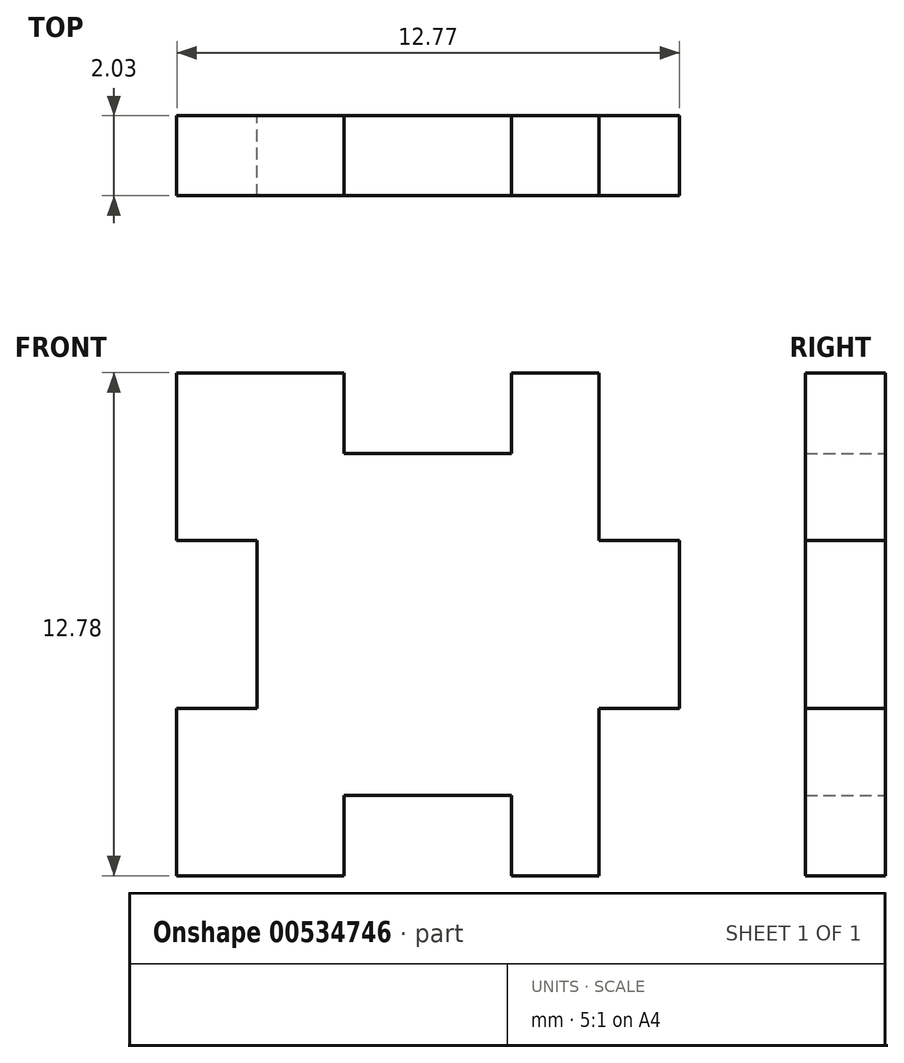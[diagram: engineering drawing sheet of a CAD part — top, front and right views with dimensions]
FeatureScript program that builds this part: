
annotation { "Feature Type Name" : "Feature", "Feature Type Description" : "" }
export const myFeature = defineFeature(function(context is Context, id is Id, definition is map)
    precondition{}
    {
        {
            var Q0;
            Q0=qCreatedBy(makeId("Front.planeOp"),FACE);
            var sketch = newSketch(context, id + "F0", { "sketchPlane" : qUnion([Q0])});
            skLineSegment(sketch, "E0", {"start": v(-10.99, 26.89) * mm, "end": v(-10.99, 29.02) * mm});
            skLineSegment(sketch, "E1", {"start": v(-10.99, 29.02) * mm, "end": v(-13.03, 29.02) * mm});
            skLineSegment(sketch, "E2", {"start": v(-13.03, 29.02) * mm, "end": v(-13.03, 33.28) * mm});
            skLineSegment(sketch, "E3", {"start": v(-13.03, 33.28) * mm, "end": v(-8.78, 33.28) * mm});
            skLineSegment(sketch, "E4", {"start": v(-8.78, 33.28) * mm, "end": v(-8.78, 31.23) * mm});
            skLineSegment(sketch, "E5", {"start": v(-8.78, 31.23) * mm, "end": v(-4.53, 31.23) * mm});
            skLineSegment(sketch, "E6", {"start": v(-4.53, 31.23) * mm, "end": v(-4.53, 33.28) * mm});
            skLineSegment(sketch, "E7", {"start": v(-4.53, 33.28) * mm, "end": v(-2.3, 33.28) * mm});
            skLineSegment(sketch, "E8", {"start": v(-2.3, 33.28) * mm, "end": v(-2.3, 29.02) * mm});
            skLineSegment(sketch, "E9", {"start": v(-2.3, 29.02) * mm, "end": v(-0.26, 29.02) * mm});
            skLineSegment(sketch, "E10", {"start": v(-10.99, 26.89) * mm, "end": v(8.72, 26.89) * mm, "construction": true});
            skLineSegment(sketch, "E11.MirrorCS", {"start": v(-2.3, 24.76) * mm, "end": v(-0.26, 24.76) * mm});
            skLineSegment(sketch, "E12.MirrorCS", {"start": v(-2.3, 20.5) * mm, "end": v(-2.3, 24.76) * mm});
            skLineSegment(sketch, "E13.MirrorCS", {"start": v(-4.53, 20.5) * mm, "end": v(-2.3, 20.5) * mm});
            skLineSegment(sketch, "E14.MirrorCS", {"start": v(-4.53, 22.55) * mm, "end": v(-4.53, 20.5) * mm});
            skLineSegment(sketch, "E15.MirrorCS", {"start": v(-8.78, 22.55) * mm, "end": v(-4.53, 22.55) * mm});
            skLineSegment(sketch, "E16.MirrorCS", {"start": v(-8.78, 20.5) * mm, "end": v(-8.78, 22.55) * mm});
            skLineSegment(sketch, "E17.MirrorCS", {"start": v(-13.03, 20.5) * mm, "end": v(-8.78, 20.5) * mm});
            skLineSegment(sketch, "E18.MirrorCS", {"start": v(-13.03, 24.76) * mm, "end": v(-13.03, 20.5) * mm});
            skLineSegment(sketch, "E19.MirrorCS", {"start": v(-10.99, 24.76) * mm, "end": v(-13.03, 24.76) * mm});
            skLineSegment(sketch, "E20.MirrorCS", {"start": v(-10.99, 26.89) * mm, "end": v(-10.99, 24.76) * mm});
            skLineSegment(sketch, "E21", {"start": v(-0.26, 29.02) * mm, "end": v(-0.26, 24.76) * mm});
            skSolve(sketch);
        }
        {
            var Q0;
            Q0=makeQuery(id+"F0.imprint","IMPRINT",FACE,{"disambiguationData":[TD([[makeQuery(id+"F0.imprint","IMPRINT",EDGE,{"derivedFrom":sQuery(id+"F0.wireOp",EDGE,"E0")}),-1.0]])]});
            extrude(context, id + "F1", {"entities" : qUnion([Q0]), "depth" : 2.03 * mm, "offsetDistance" : 25.4 * mm});
        }
        {
            var Q0;
            Q0=qCreatedBy(makeId("Front.planeOp"),FACE);
            cPlane(context, id + "F2", {"entities" : qUnion([Q0]), "cplaneType" : CPlaneType.OFFSET, "offset" : 4.06 * mm, "width" : 152.4 * mm, "height" : 152.4 * mm});
        }
        {
            var Q0;
            Q0=qCreatedBy(id+"F2.planeOp",FACE);
            var sketch = newSketch(context, id + "F3", { "sketchPlane" : qUnion([Q0])});
            skText(sketch, "E22", { "text": "N", "fontName": "OpenSans-Regular.ttf"});
            const initialGuessF3  = {"E22": [-0.0091, 0.02434, 1, 0, 0.00553]};
            skSetInitialGuess(sketch, initialGuessF3);
            skSolve(sketch);
        }
        {
            var Q0;
            Q0 = qSketchRegion(id + "F3", true);
            extrude(context, id + "F4", {"entities" : qUnion([Q0]), "operationType" : NewBodyOperationType.REMOVE, "oppositeDirection" : true, "depth" : 0.5 * mm, "offsetDistance" : 25.4 * mm});
        }
    });
